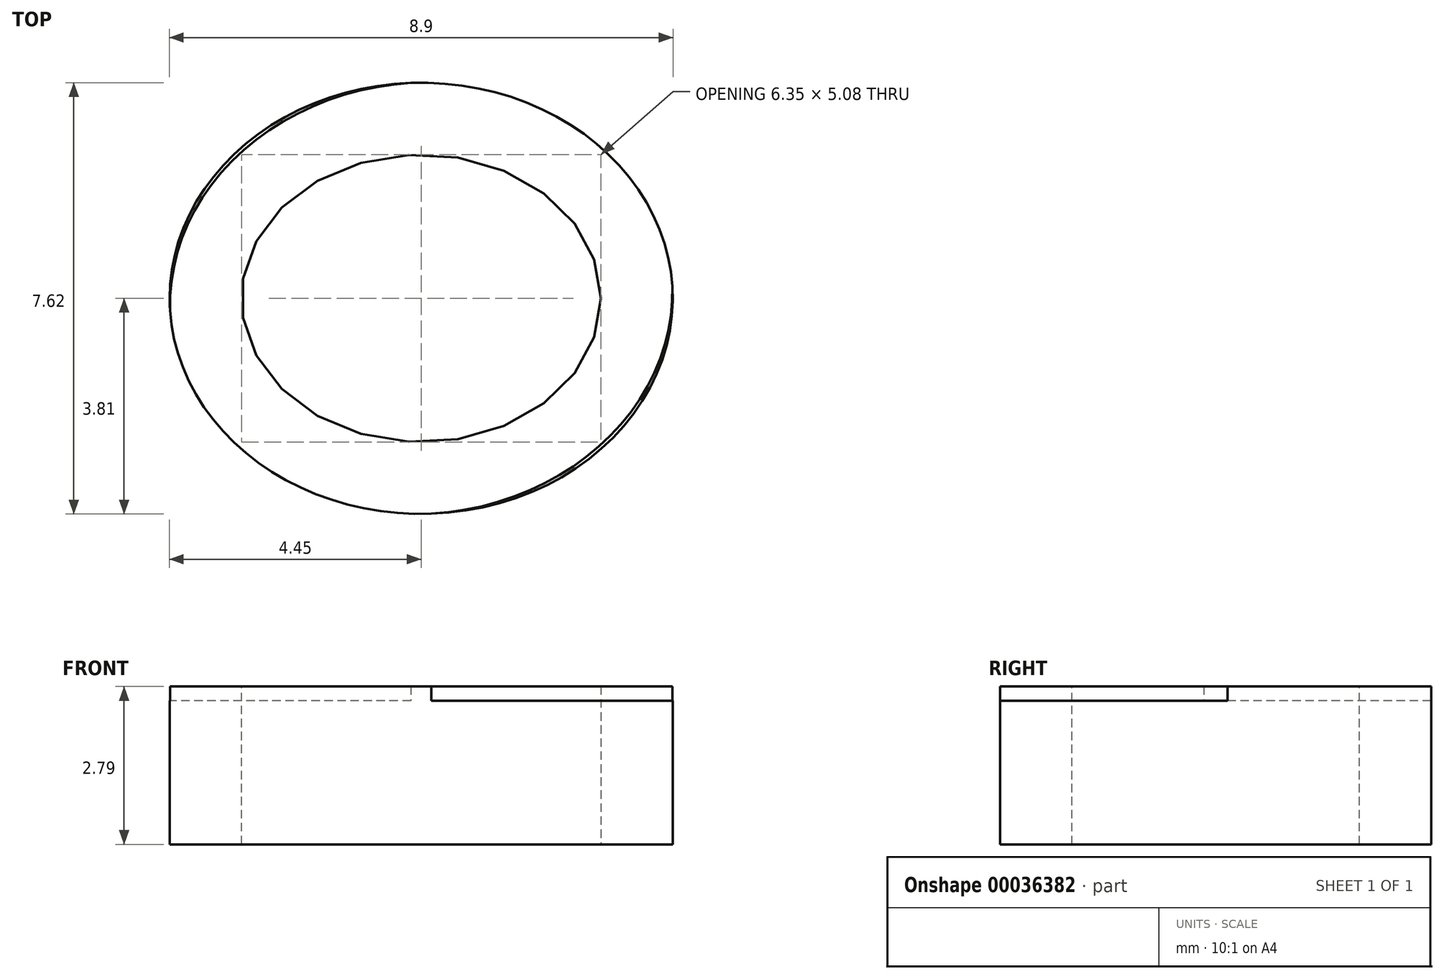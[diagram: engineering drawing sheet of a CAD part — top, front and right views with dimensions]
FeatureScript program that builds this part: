
annotation { "Feature Type Name" : "Feature", "Feature Type Description" : "" }
export const myFeature = defineFeature(function(context is Context, id is Id, definition is map)
    precondition{}
    {
        {
            var Q0;
            Q0=qCreatedBy(makeId("Top.planeOp"),FACE);
            var sketch = newSketch(context, id + "F0", { "sketchPlane" : qUnion([Q0])});
            skEllipse(sketch, "E0", {"center": v(0, 0) * mm, "majorRadius": 4.45 * mm, "minorRadius": 3.81 * mm, "majorAxis": v(-1, 0)});
            skSolve(sketch);
        }
        {
            var Q0;
            Q0=makeQuery(id+"F0.imprint","IMPRINT",FACE,{"disambiguationData":[TD([[makeQuery(id+"F0.imprint","IMPRINT",EDGE,{"derivedFrom":sQuery(id+"F0.wireOp",EDGE,"E0")}),1.0]])]});
            extrude(context, id + "F1", {"entities" : qUnion([Q0]), "depth" : 1.27 * mm});
        }
        {
            var Q0;
            Q0=makeQuery(id+"F1.opExtrude","CAP_FACE",FACE,{"disambiguationData":[OSD([sQuery(id+"F0.wireOp",EDGE,"E0")])],"isStart":false});
            var sketch = newSketch(context, id + "F2", { "sketchPlane" : qUnion([Q0])});
            skEllipse(sketch, "E1", {"center": v(0, 0) * mm, "majorRadius": 4.45 * mm, "minorRadius": 3.81 * mm, "majorAxis": v(1, 0)});
            skEllipse(sketch, "E2", {"center": v(0, 0) * mm, "majorRadius": 3.18 * mm, "minorRadius": 2.54 * mm, "majorAxis": v(1, 0)});
            skSolve(sketch);
        }
        {
            var Q0;
            Q0=makeQuery(id+"F2.imprint","IMPRINT",FACE,{"disambiguationData":[TD([[makeQuery(id+"F2.imprint","IMPRINT",EDGE,{"derivedFrom":sQuery(id+"F2.wireOp",EDGE,"E1")}),1.0]])]});
            extrude(context, id + "F3", {"entities" : qUnion([Q0]), "operationType" : NewBodyOperationType.ADD, "depth" : 1.27 * mm});
        }
        {
            var Q0;
            Q0=makeQuery(id+"F3.opExtrude","CAP_FACE",FACE,{"disambiguationData":[OSD([sQuery(id+"F2.wireOp",EDGE,"E1"),sQuery(id+"F2.wireOp",EDGE,"E2")])],"isStart":false});
            var sketch = newSketch(context, id + "F4", { "sketchPlane" : qUnion([Q0])});
            skEllipse(sketch, "E3", {"center": v(0, 0) * mm, "majorRadius": 4.45 * mm, "minorRadius": 3.81 * mm, "majorAxis": v(1, 0.1)});
            skSolve(sketch);
        }
        {
            var Q0;
            Q0=makeQuery(id+"F4.imprint","IMPRINT",FACE,{"disambiguationData":[TD([[makeQuery(id+"F4.imprint","IMPRINT",EDGE,{"derivedFrom":makeQuery(id+"F3.opExtrude","CAP_EDGE",EDGE,{"disambiguationData":[OSD([sQuery(id+"F2.wireOp",EDGE,"E2")])],"isStart":false})}),-1.0]])]});
            var Q1;
            Q1=makeQuery(id+"F4.imprint","IMPRINT",FACE,{"disambiguationData":[TD([[makeQuery(id+"F4.imprint","IMPRINT",EDGE,{"derivedFrom":makeQuery(id+"F3.opExtrude","CAP_EDGE",EDGE,{"disambiguationData":[OSD([sQuery(id+"F2.wireOp",EDGE,"E2")])],"isStart":false})}),1.0]])]});
            extrude(context, id + "F5", {"entities" : qUnion([Q0, Q1]), "operationType" : NewBodyOperationType.ADD, "depth" : 0.25 * mm});
        }
        {
            var Q0;
            Q0=makeQuery(id+"F5.opExtrude","CAP_FACE",FACE,{"disambiguationData":[OSD([sQuery(id+"F2.wireOp",EDGE,"E1"),sQuery(id+"F4.wireOp",EDGE,"E3")])],"isStart":false});
            var sketch = newSketch(context, id + "F6", { "sketchPlane" : qUnion([Q0])});
            skEllipse(sketch, "E4", {"center": v(0, 0) * mm, "majorRadius": 3.18 * mm, "minorRadius": 2.54 * mm, "majorAxis": v(1, 0)});
            skSolve(sketch);
        }
        {
            var Q0;
            Q0=makeQuery(id+"F6.imprint","IMPRINT",FACE,{"disambiguationData":[TD([[makeQuery(id+"F6.imprint","IMPRINT",EDGE,{"derivedFrom":sQuery(id+"F6.wireOp",EDGE,"E4")}),1.0]])]});
            extrude(context, id + "F7", {"entities" : qUnion([Q0]), "operationType" : NewBodyOperationType.REMOVE, "oppositeDirection" : true, "depth" : 25.4 * mm});
        }
    });
